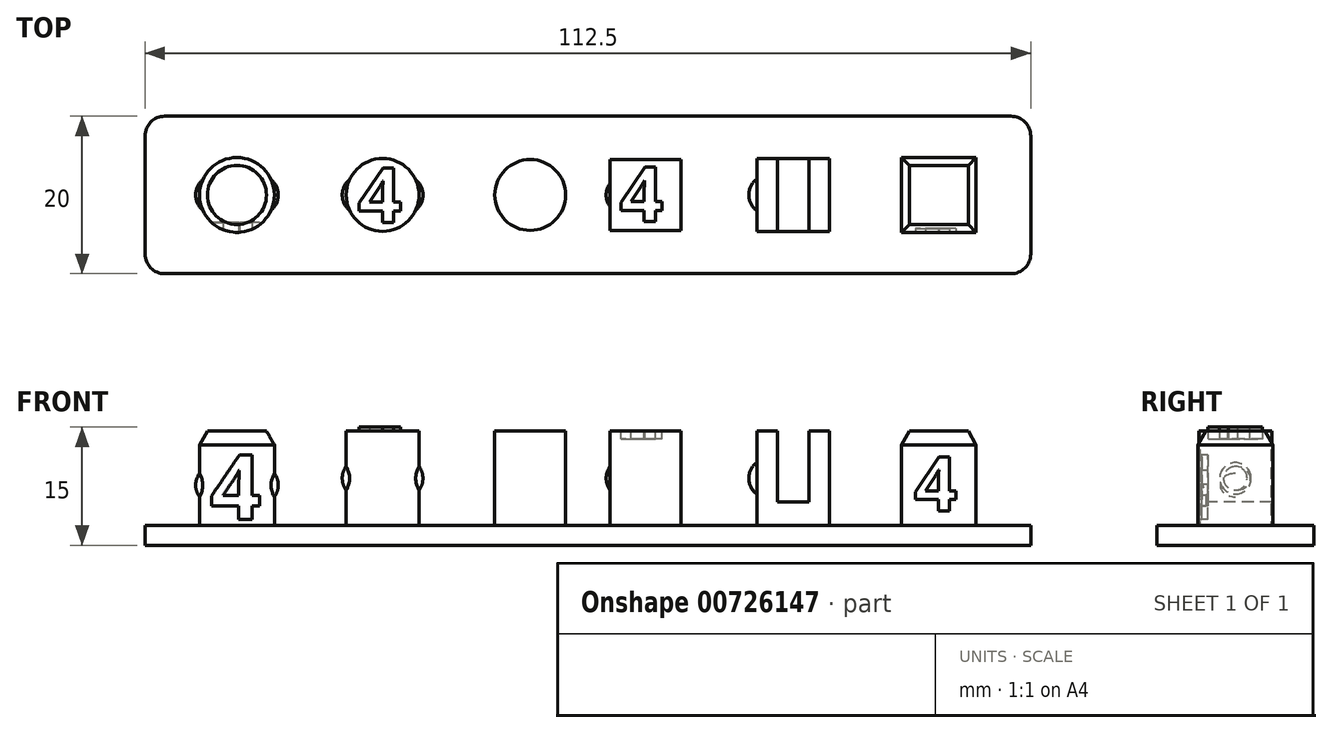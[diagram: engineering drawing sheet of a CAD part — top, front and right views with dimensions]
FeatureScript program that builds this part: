
annotation { "Feature Type Name" : "Feature", "Feature Type Description" : "" }
export const myFeature = defineFeature(function(context is Context, id is Id, definition is map)
    precondition{}
    {
        {
            var Q0;
            Q0=qCreatedBy(makeId("Top.planeOp"),FACE);
            var sketch = newSketch(context, id + "F0", { "sketchPlane" : qUnion([Q0])});
            skLineSegment(sketch, "E0.bottom", {"start": v(56.25, -10) * mm, "end": v(-56.25, -10) * mm});
            skLineSegment(sketch, "E0.top", {"start": v(56.25, 10) * mm, "end": v(-56.25, 10) * mm});
            skLineSegment(sketch, "E0.left", {"start": v(56.25, -10) * mm, "end": v(56.25, 10) * mm});
            skLineSegment(sketch, "E0.right", {"start": v(-56.25, -10) * mm, "end": v(-56.25, 10) * mm});
            skPoint(sketch, "E0.middle", {"position": v(0, 0) * mm});
            skSolve(sketch);
        }
        {
            var Q0;
            Q0=makeQuery(id+"F0.imprint","IMPRINT",FACE,{"disambiguationData":[TD([[makeQuery(id+"F0.imprint","IMPRINT",EDGE,{"derivedFrom":sQuery(id+"F0.wireOp",EDGE,"E0.bottom")}),-1.0]])]});
            extrude(context, id + "F1", {"entities" : qUnion([Q0]), "depth" : 2.5 * mm, "offsetDistance" : 25 * mm});
        }
        {
            var Q0;
            Q0=makeQuery(id+"F1.opExtrude","CAP_FACE",FACE,{"disambiguationData":[OSD([sQuery(id+"F0.wireOp",EDGE,"E0.bottom"),sQuery(id+"F0.wireOp",EDGE,"E0.top"),sQuery(id+"F0.wireOp",EDGE,"E0.left"),sQuery(id+"F0.wireOp",EDGE,"E0.right")])],"isStart":false});
            var sketch = newSketch(context, id + "F2", { "sketchPlane" : qUnion([Q0])});
            skLineSegment(sketch, "E1.bottom", {"start": v(30.7, -4.62) * mm, "end": v(21.45, -4.62) * mm});
            skLineSegment(sketch, "E1.top", {"start": v(30.7, 4.63) * mm, "end": v(21.45, 4.63) * mm});
            skLineSegment(sketch, "E1.left", {"start": v(30.7, -4.62) * mm, "end": v(30.7, 4.63) * mm});
            skLineSegment(sketch, "E1.right", {"start": v(21.45, -4.62) * mm, "end": v(21.45, 4.63) * mm});
            skPoint(sketch, "E1.middle", {"position": v(26.07, 0) * mm});
            skLineSegment(sketch, "E2.bottom", {"start": v(39.83, -4.75) * mm, "end": v(49.33, -4.75) * mm});
            skLineSegment(sketch, "E2.top", {"start": v(39.83, 4.75) * mm, "end": v(49.33, 4.75) * mm});
            skLineSegment(sketch, "E2.left", {"start": v(39.83, -4.75) * mm, "end": v(39.83, 4.75) * mm});
            skLineSegment(sketch, "E2.right", {"start": v(49.33, -4.75) * mm, "end": v(49.33, 4.75) * mm});
            skPoint(sketch, "E2.middle", {"position": v(44.58, 0) * mm});
            skCircle(sketch, "E3", {"center": v(-7.33, 0) * mm, "radius": 4.5 * mm});
            skCircle(sketch, "E4", {"center": v(-26.07, 0) * mm, "radius": 4.62 * mm});
            skLineSegment(sketch, "E5.bottom", {"start": v(11.83, -4.5) * mm, "end": v(2.82, -4.5) * mm});
            skLineSegment(sketch, "E5.top", {"start": v(11.83, 4.5) * mm, "end": v(2.82, 4.5) * mm});
            skLineSegment(sketch, "E5.left", {"start": v(11.83, -4.5) * mm, "end": v(11.83, 4.5) * mm});
            skLineSegment(sketch, "E5.right", {"start": v(2.82, -4.5) * mm, "end": v(2.82, 4.5) * mm});
            skPoint(sketch, "E5.middle", {"position": v(7.33, 0) * mm});
            skCircle(sketch, "E6", {"center": v(-44.58, 0) * mm, "radius": 4.75 * mm});
            skSolve(sketch);
        }
        {
            var Q0;
            Q0 = qSketchRegion(id + "F2", true);
            extrude(context, id + "F3", {"entities" : qUnion([Q0]), "operationType" : NewBodyOperationType.ADD, "depth" : 12 * mm, "offsetDistance" : 25 * mm});
        }
        {
            var Q0;
            Q0=makeQuery(id+"F1.opExtrude","SWEPT_EDGE",EDGE,{"disambiguationData":[OSD([sQuery(id+"F0.wireOp",EDGE,"E0.bottom"),sQuery(id+"F0.wireOp",EDGE,"E0.left")])]});
            var Q1;
            Q1=makeQuery(id+"F1.opExtrude","SWEPT_EDGE",EDGE,{"disambiguationData":[OSD([sQuery(id+"F0.wireOp",EDGE,"E0.top"),sQuery(id+"F0.wireOp",EDGE,"E0.left")])]});
            var Q2;
            Q2=makeQuery(id+"F1.opExtrude","SWEPT_EDGE",EDGE,{"disambiguationData":[OSD([sQuery(id+"F0.wireOp",EDGE,"E0.bottom"),sQuery(id+"F0.wireOp",EDGE,"E0.right")])]});
            var Q3;
            Q3=makeQuery(id+"F1.opExtrude","SWEPT_EDGE",EDGE,{"disambiguationData":[OSD([sQuery(id+"F0.wireOp",EDGE,"E0.top"),sQuery(id+"F0.wireOp",EDGE,"E0.right")])]});
            fillet(context, id + "F4", {"entities" : qUnion([Q0, Q1, Q2, Q3]), "radius" : 2.5 * mm, "tangentPropagation" : true, "allowEdgeOverflow" : false});
        }
        {
            var Q0;
            Q0=makeQuery(id+"F3.opExtrude","SWEPT_FACE",FACE,{"disambiguationData":[OSD([sQuery(id+"F2.wireOp",EDGE,"E1.bottom")])]});
            var sketch = newSketch(context, id + "F5", { "sketchPlane" : qUnion([Q0])});
            skLineSegment(sketch, "E7.bottom", {"start": v(24.07, 14.5) * mm, "end": v(28.08, 14.5) * mm});
            skLineSegment(sketch, "E7.top", {"start": v(24.07, 5.5) * mm, "end": v(28.08, 5.5) * mm});
            skLineSegment(sketch, "E7.left", {"start": v(24.07, 14.5) * mm, "end": v(24.07, 5.5) * mm});
            skLineSegment(sketch, "E7.right", {"start": v(28.08, 14.5) * mm, "end": v(28.08, 5.5) * mm});
            skPoint(sketch, "E8.endSnap0", {"position": v(26.07, 2.5) * mm});
            skLineSegment(sketch, "E9", {"start": v(26.07, 2.5) * mm, "end": v(26.07, 5.5) * mm});
            skArc(sketch, "E10", {"start": v(21.45, 10.5) * mm, "mid": v(20.45, 8.5) * mm, "end": v(21.45, 6.5) * mm});
            skLineSegment(sketch, "E11", {"start": v(21.45, 6.5) * mm, "end": v(21.45, 10.5) * mm});
            skArc(sketch, "E12.MirrorCS", {"start": v(30.7, 10.5) * mm, "mid": v(31.7, 8.5) * mm, "end": v(30.7, 6.5) * mm});
            skLineSegment(sketch, "E13.MirrorCS", {"start": v(30.7, 6.5) * mm, "end": v(30.7, 10.5) * mm});
            skSolve(sketch);
        }
        {
            var Q0;
            Q0=makeQuery(id+"F5.imprint","IMPRINT",FACE,{"disambiguationData":[TD([[makeQuery(id+"F5.imprint","IMPRINT",EDGE,{"derivedFrom":sQuery(id+"F5.wireOp",EDGE,"E7.bottom")}),1.0]])]});
            extrude(context, id + "F6", {"entities" : qUnion([Q0]), "operationType" : NewBodyOperationType.REMOVE, "oppositeDirection" : true, "depth" : 25 * mm, "offsetDistance" : 25 * mm});
        }
        {
            var Q0;
            Q0=qCreatedBy(makeId("Front.planeOp"),FACE);
            var sketch = newSketch(context, id + "F7", { "sketchPlane" : qUnion([Q0])});
            skArc(sketch, "E14.0", {"start": v(20.45, 8.5) * mm, "mid": v(20.71, 7.38) * mm, "end": v(21.45, 6.5) * mm});
            skLineSegment(sketch, "E14.1", {"start": v(21.45, 6.5) * mm, "end": v(21.45, 8.5) * mm});
            skArc(sketch, "E14.2", {"start": v(31.7, 8.5) * mm, "mid": v(31.44, 7.38) * mm, "end": v(30.7, 6.5) * mm});
            skLineSegment(sketch, "E14.3", {"start": v(30.7, 6.5) * mm, "end": v(30.7, 8.5) * mm});
            skLineSegment(sketch, "E15", {"start": v(21.45, 8.5) * mm, "end": v(20.45, 8.5) * mm});
            skLineSegment(sketch, "E16", {"start": v(30.7, 8.5) * mm, "end": v(31.7, 8.5) * mm});
            skPoint(sketch, "E17.orphan", {"position": v(21.45, 10.5) * mm});
            skPoint(sketch, "E18.orphan", {"position": v(30.7, 10.5) * mm});
            skSolve(sketch);
        }
        {
            var Q0;
            Q0=makeQuery(id+"F7.imprint","IMPRINT",FACE,{"disambiguationData":[TD([[makeQuery(id+"F7.imprint","IMPRINT",EDGE,{"derivedFrom":sQuery(id+"F7.wireOp",EDGE,"E14.0")}),1.0]])]});
            var Q1;
            Q1=makeQuery(id+"F7.imprint","IMPRINT",FACE,{"disambiguationData":[TD([[makeQuery(id+"F7.imprint","IMPRINT",EDGE,{"derivedFrom":sQuery(id+"F7.wireOp",EDGE,"E14.2")}),-1.0]])]});
            var Q2;
            Q2=sQuery(id+"F7.wireOp",EDGE,"E15");
            revolve(context, id + "F8", {"operationType" : NewBodyOperationType.ADD, "surfaceOperationType" : NewSurfaceOperationType.NEW, "entities" : qUnion([Q0, Q1]), "axis" : qUnion([Q2]), "revolveType" : RevolveType.FULL});
        }
        {
            var Q0;
            Q0=qCreatedBy(makeId("Front.planeOp"),FACE);
            var sketch = newSketch(context, id + "F9", { "sketchPlane" : qUnion([Q0])});
            skLineSegment(sketch, "E19.0", {"start": v(2.82, 14.5) * mm, "end": v(2.82, 10) * mm, "construction": true});
            skLineSegment(sketch, "E20.0", {"start": v(11.83, 14.5) * mm, "end": v(11.83, 2.5) * mm, "construction": true});
            skLineSegment(sketch, "E21", {"start": v(2.82, 2.5) * mm, "end": v(11.83, 2.5) * mm, "construction": true});
            skLineSegment(sketch, "E22", {"start": v(7.33, 2.5) * mm, "end": v(7.33, 16.09) * mm, "construction": true});
            skArc(sketch, "E23", {"start": v(2.32, 8.5) * mm, "mid": v(2.45, 7.7) * mm, "end": v(2.83, 7) * mm});
            skPoint(sketch, "E23.centerSnap0", {"position": v(2.82, 8.5) * mm});
            skLineSegment(sketch, "E24", {"start": v(2.82, 7) * mm, "end": v(2.82, 10) * mm});
            skLineSegment(sketch, "E25", {"start": v(2.82, 8.5) * mm, "end": v(2.32, 8.5) * mm});
            skLineSegment(sketch, "E26.trimOffspring", {"start": v(2.82, 8.5) * mm, "end": v(2.82, 2.5) * mm, "construction": true});
            skSolve(sketch);
        }
        {
            var Q0;
            {var subQ0=sQuery(id+"F9.wireOp",EDGE,"E23");Q0=makeQuery(id+"F9.imprint","IMPRINT",FACE,{"disambiguationData":[TD([[makeQuery(id+"F9.imprint","IMPRINT",EDGE,{"derivedFrom":subQ0}),1.0]])]});}
            var Q1;
            Q1=sQuery(id+"F9.wireOp",EDGE,"E25");
            revolve(context, id + "F10", {"operationType" : NewBodyOperationType.ADD, "surfaceOperationType" : NewSurfaceOperationType.NEW, "entities" : qUnion([Q0]), "axis" : qUnion([Q1]), "revolveType" : RevolveType.FULL});
        }
        {
            var Q0;
            Q0=makeQuery(id+"F3.opExtrude","CAP_EDGE",EDGE,{"disambiguationData":[OSD([sQuery(id+"F2.wireOp",EDGE,"E2.bottom")])],"isStart":false});
            var Q1;
            Q1=makeQuery(id+"F3.opExtrude","CAP_EDGE",EDGE,{"disambiguationData":[OSD([sQuery(id+"F2.wireOp",EDGE,"E2.right")])],"isStart":false});
            var Q2;
            Q2=makeQuery(id+"F3.opExtrude","CAP_EDGE",EDGE,{"disambiguationData":[OSD([sQuery(id+"F2.wireOp",EDGE,"E2.top")])],"isStart":false});
            var Q3;
            Q3=makeQuery(id+"F3.opExtrude","CAP_EDGE",EDGE,{"disambiguationData":[OSD([sQuery(id+"F2.wireOp",EDGE,"E2.left")])],"isStart":false});
            var Q4;
            Q4=makeQuery(id+"F3.opExtrude","CAP_EDGE",EDGE,{"disambiguationData":[OSD([sQuery(id+"F2.wireOp",EDGE,"E6")])],"isStart":false});
            chamfer(context, id + "F11", {"entities" : qUnion([Q0, Q1, Q2, Q3, Q4]), "chamferType" : ChamferType.OFFSET_ANGLE, "width" : 1 * mm, "oppositeDirection" : false, "angle" : 60 * degree, "tangentPropagation" : true});
        }
        {
            var Q0;
            Q0=makeQuery(id+"F3.opExtrude","CAP_FACE",FACE,{"disambiguationData":[OSD([sQuery(id+"F2.wireOp",EDGE,"E4")])],"isStart":false});
            var sketch = newSketch(context, id + "F12", { "sketchPlane" : qUnion([Q0])});
            skText(sketch, "E27", { "text": "4", "fontName": "OpenSans-Bold.ttf"});
            skText(sketch, "E28", { "text": "4", "fontName": "OpenSans-Bold.ttf"});
            const initialGuessF12  = {"E27": [0.00403, -0.0034, 1, 0, 0.00698], "E28": [-0.0292, -0.00349, 1, 0, 0.00698]};
            skSetInitialGuess(sketch, initialGuessF12);
            skSolve(sketch);
        }
        {
            var Q0;
            Q0=makeQuery(id+"F12.imprint","IMPRINT",FACE,{"disambiguationData":[TD([[makeQuery(id+"F12.imprint","IMPRINT",EDGE,{"derivedFrom":sQuery(id+"F12.wireOp",EDGE,"E28.sketch_text.stroke-0")}),-1.0]])]});
            extrude(context, id + "F13", {"entities" : qUnion([Q0]), "operationType" : NewBodyOperationType.ADD, "depth" : .5 * mm, "offsetDistance" : 25 * mm});
        }
        {
            var Q0;
            Q0=makeQuery(id+"F12.imprint","IMPRINT",FACE,{"disambiguationData":[TD([[makeQuery(id+"F12.imprint","IMPRINT",EDGE,{"derivedFrom":sQuery(id+"F12.wireOp",EDGE,"E27.sketch_text.stroke-0")}),-1.0]])]});
            extrude(context, id + "F14", {"entities" : qUnion([Q0]), "operationType" : NewBodyOperationType.REMOVE, "oppositeDirection" : true, "depth" : 1 * mm, "offsetDistance" : 25 * mm});
        }
        {
            var Q0;
            Q0=makeQuery(id+"F3.opExtrude","SWEPT_FACE",FACE,{"disambiguationData":[OSD([sQuery(id+"F2.wireOp",EDGE,"E2.bottom")])]});
            var sketch = newSketch(context, id + "F15", { "sketchPlane" : qUnion([Q0])});
            skText(sketch, "E29", { "text": "4", "fontName": "OpenSans-Bold.ttf"});
            const initialGuessF15  = {"E29": [0.04143, 0.00437, 1, 0, 0.00691]};
            skSetInitialGuess(sketch, initialGuessF15);
            skSolve(sketch);
        }
        {
            var Q0;
            Q0=makeQuery(id+"F15.imprint","IMPRINT",FACE,{"disambiguationData":[TD([[makeQuery(id+"F15.imprint","IMPRINT",EDGE,{"derivedFrom":sQuery(id+"F15.wireOp",EDGE,"E29.sketch_text.stroke-0")}),-1.0]])]});
            extrude(context, id + "F16", {"entities" : qUnion([Q0]), "operationType" : NewBodyOperationType.REMOVE, "oppositeDirection" : true, "depth" : .5 * mm, "offsetDistance" : 25 * mm});
        }
        {
            var Q0;
            Q0=makeQuery(id+"F1.opExtrude","SWEPT_FACE",FACE,{"disambiguationData":[OSD([sQuery(id+"F0.wireOp",EDGE,"E0.bottom")])]});
            var sketch = newSketch(context, id + "F17", { "sketchPlane" : qUnion([Q0])});
            skText(sketch, "E30", { "text": "4", "fontName": "OpenSans-Bold.ttf"});
            const initialGuessF17  = {"E30": [-0.04804, 0.0033, 1, 0, 0.00826]};
            skSetInitialGuess(sketch, initialGuessF17);
            skSolve(sketch);
        }
        {
            var Q0;
            Q0=makeQuery(id+"F17.imprint","IMPRINT",FACE,{"disambiguationData":[TD([[makeQuery(id+"F17.imprint","IMPRINT",EDGE,{"derivedFrom":sQuery(id+"F17.wireOp",EDGE,"E30.sketch_text.stroke-0")}),-1.0]])]});
            extrude(context, id + "F18", {"entities" : qUnion([Q0]), "operationType" : NewBodyOperationType.REMOVE, "oppositeDirection" : true, "depth" : 6.5 * mm, "offsetDistance" : 25 * mm});
        }
        {
            var Q0;
            Q0=qCreatedBy(makeId("Front.planeOp"),FACE);
            var sketch = newSketch(context, id + "F19", { "sketchPlane" : qUnion([Q0])});
            skLineSegment(sketch, "E31.0", {"start": v(-39.83, 12.77) * mm, "end": v(-49.33, 12.77) * mm, "construction": true});
            skLineSegment(sketch, "E32.0", {"start": v(53.75, 2.5) * mm, "end": v(-53.75, 2.5) * mm});
            skLineSegment(sketch, "E33", {"start": v(-49.33, 12.77) * mm, "end": v(-49.33, 2.5) * mm});
            skArc(sketch, "E34", {"start": v(-49.83, 7.63) * mm, "mid": v(-49.1, 5.87) * mm, "end": v(-47.32, 5.13) * mm});
            skPoint(sketch, "E34.centerSnap0", {"position": v(-49.33, 7.63) * mm});
            skLineSegment(sketch, "E35", {"start": v(-47.32, 7.63) * mm, "end": v(-49.83, 7.63) * mm});
            skLineSegment(sketch, "E36", {"start": v(-47.32, 7.63) * mm, "end": v(-47.32, 5.13) * mm});
            skPoint(sketch, "E37.orphan", {"position": v(-47.32, 10.13) * mm});
            skLineSegment(sketch, "E38", {"start": v(-39.83, 12.77) * mm, "end": v(-39.83, 2.5) * mm, "construction": true});
            skLineSegment(sketch, "E39", {"start": v(-44.58, 12.77) * mm, "end": v(-44.58, 2.5) * mm, "construction": true});
            skPoint(sketch, "E40.MirrorP", {"position": v(-39.83, 7.63) * mm});
            skLineSegment(sketch, "E41.MirrorCS", {"start": v(-41.83, 7.63) * mm, "end": v(-39.33, 7.63) * mm});
            skLineSegment(sketch, "E42.MirrorCS", {"start": v(-41.83, 7.63) * mm, "end": v(-41.83, 5.13) * mm});
            skArc(sketch, "E43.MirrorCS", {"start": v(-39.33, 7.63) * mm, "mid": v(-40.06, 5.87) * mm, "end": v(-41.83, 5.13) * mm});
            skSolve(sketch);
        }
        {
            var Q0;
            Q0 = qSketchRegion(id + "F19", true);
            var Q1;
            Q1=sQuery(id+"F19.wireOp",EDGE,"E35");
            revolve(context, id + "F20", {"operationType" : NewBodyOperationType.ADD, "surfaceOperationType" : NewSurfaceOperationType.NEW, "entities" : qUnion([Q0]), "axis" : qUnion([Q1]), "revolveType" : RevolveType.FULL});
        }
        {
            var Q0;
            Q0=qCreatedBy(makeId("Front.planeOp"),FACE);
            var sketch = newSketch(context, id + "F21", { "sketchPlane" : qUnion([Q0])});
            skLineSegment(sketch, "E44.0", {"start": v(-21.2, 14.5) * mm, "end": v(-30.7, 14.5) * mm, "construction": true});
            skArc(sketch, "E45", {"start": v(-31.2, 8.5) * mm, "mid": v(-30.47, 6.73) * mm, "end": v(-28.7, 6) * mm});
            skPoint(sketch, "E45.centerSnap0", {"position": v(-30.7, 8.5) * mm});
            skLineSegment(sketch, "E46", {"start": v(-28.7, 8.5) * mm, "end": v(-31.2, 8.5) * mm});
            skLineSegment(sketch, "E47", {"start": v(-28.7, 8.5) * mm, "end": v(-28.7, 6) * mm});
            skPoint(sketch, "E48.orphan", {"position": v(-28.7, 11) * mm});
            skLineSegment(sketch, "E49.0", {"start": v(53.75, 2.5) * mm, "end": v(-53.75, 2.5) * mm});
            skLineSegment(sketch, "E50.0", {"start": v(-30.7, 14.5) * mm, "end": v(-21.45, 14.5) * mm, "construction": true});
            skLineSegment(sketch, "E51", {"start": v(-26.07, 14.5) * mm, "end": v(-26.07, 8.16) * mm, "construction": true});
            skPoint(sketch, "E52.MirrorP", {"position": v(-23.45, 11) * mm});
            skLineSegment(sketch, "E53.MirrorCS", {"start": v(-23.45, 8.5) * mm, "end": v(-23.45, 6) * mm});
            skLineSegment(sketch, "E54.MirrorCS", {"start": v(-23.45, 8.5) * mm, "end": v(-20.95, 8.5) * mm});
            skPoint(sketch, "E55.MirrorP", {"position": v(-21.45, 8.5) * mm});
            skArc(sketch, "E56.MirrorCS", {"start": v(-20.95, 8.5) * mm, "mid": v(-21.68, 6.73) * mm, "end": v(-23.45, 6) * mm});
            skLineSegment(sketch, "E57", {"start": v(-30.7, 14.5) * mm, "end": v(-30.7, 2.5) * mm, "construction": true});
            skLineSegment(sketch, "E58", {"start": v(-30.7, 8.5) * mm, "end": v(-28.7, 8.5) * mm});
            skSolve(sketch);
        }
        {
            var Q0;
            Q0 = qSketchRegion(id + "F21", true);
            var Q1;
            Q1=sQuery(id+"F21.wireOp",EDGE,"E46");
            revolve(context, id + "F22", {"operationType" : NewBodyOperationType.ADD, "surfaceOperationType" : NewSurfaceOperationType.NEW, "entities" : qUnion([Q0]), "axis" : qUnion([Q1]), "revolveType" : RevolveType.FULL});
        }
    });
